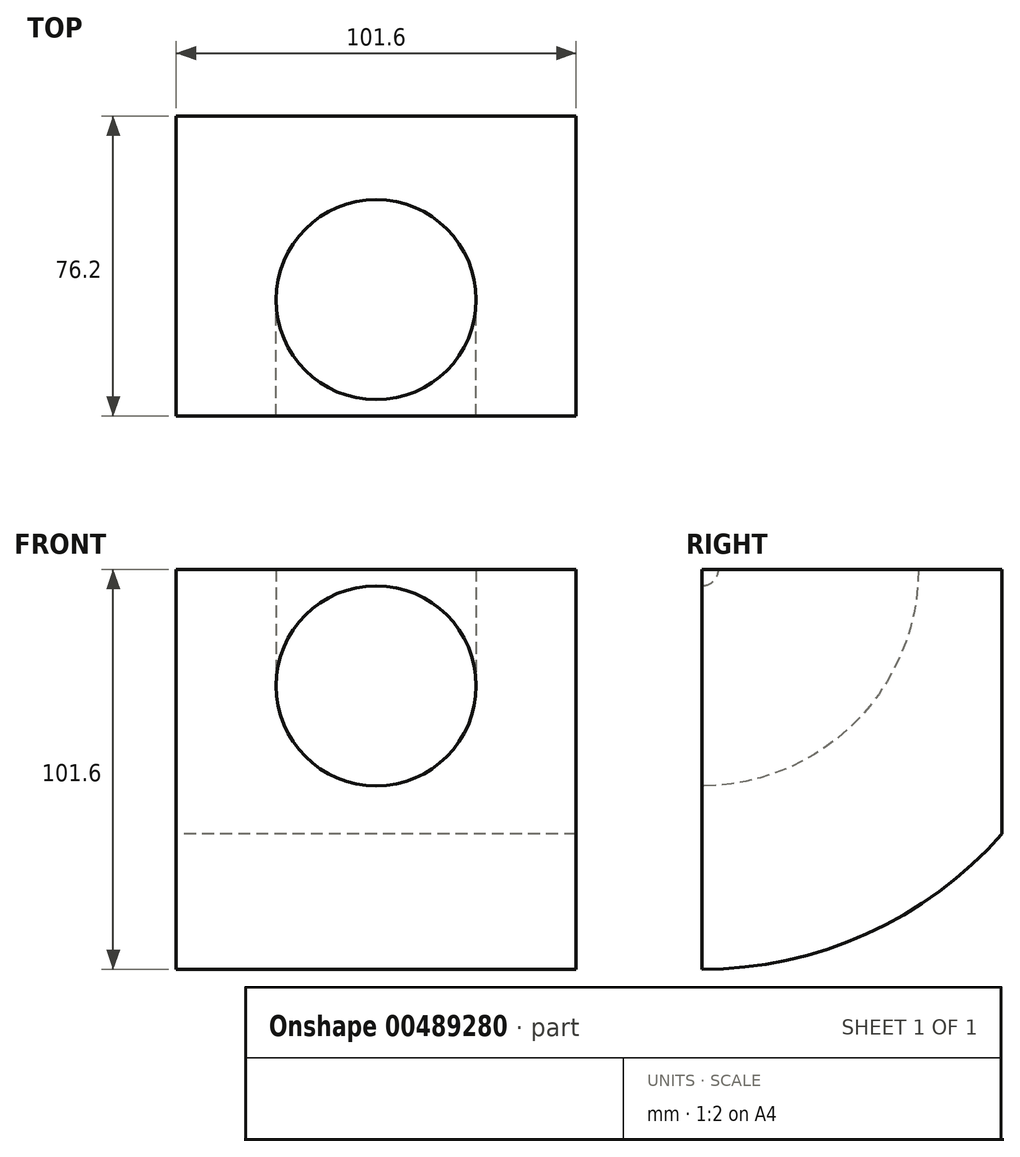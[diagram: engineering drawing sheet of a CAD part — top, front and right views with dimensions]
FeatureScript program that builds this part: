
annotation { "Feature Type Name" : "Feature", "Feature Type Description" : "" }
export const myFeature = defineFeature(function(context is Context, id is Id, definition is map)
    precondition{}
    {
        {
            var Q0;
            Q0=qCreatedBy(makeId("Front.planeOp"),FACE);
            var sketch = newSketch(context, id + "F0", { "sketchPlane" : qUnion([Q0])});
            skLineSegment(sketch, "E0.bottom", {"start": v(50.8, 87.4) * mm, "end": v(-50.8, 87.4) * mm});
            skLineSegment(sketch, "E0.top", {"start": v(50.8, -14.2) * mm, "end": v(-50.8, -14.2) * mm});
            skLineSegment(sketch, "E0.left", {"start": v(50.8, 87.4) * mm, "end": v(50.8, -14.2) * mm});
            skLineSegment(sketch, "E0.right", {"start": v(-50.8, 87.4) * mm, "end": v(-50.8, -14.2) * mm});
            skPoint(sketch, "E0.middle", {"position": v(0, 36.6) * mm});
            skSolve(sketch);
        }
        {
            var Q0;
            Q0=makeQuery(id+"F0.imprint","IMPRINT",FACE,{"disambiguationData":[TD([[makeQuery(id+"F0.imprint","IMPRINT",EDGE,{"derivedFrom":sQuery(id+"F0.wireOp",EDGE,"E0.bottom")}),1.0]])]});
            extrude(context, id + "F1", {"entities" : qUnion([Q0]), "endBound" : BoundingType.SYMMETRIC, "depth" : 76.2 * mm});
        }
        {
            var Q0;
            Q0=makeQuery(id+"F1.opExtrude","CAP_FACE",FACE,{"disambiguationData":[OSD([sQuery(id+"F0.wireOp",EDGE,"E0.bottom"),sQuery(id+"F0.wireOp",EDGE,"E0.top"),sQuery(id+"F0.wireOp",EDGE,"E0.left"),sQuery(id+"F0.wireOp",EDGE,"E0.right")])],"isStart":false});
            var sketch = newSketch(context, id + "F2", { "sketchPlane" : qUnion([Q0])});
            skCircle(sketch, "E1", {"center": v(0, 57.85) * mm, "radius": 25.4 * mm});
            skSolve(sketch);
        }
        {
            var Q0;
            Q0=makeQuery(id+"F2.imprint","IMPRINT",FACE,{"disambiguationData":[TD([[makeQuery(id+"F2.imprint","IMPRINT",EDGE,{"derivedFrom":sQuery(id+"F2.wireOp",EDGE,"E1")}),-1.0]])]});
            var Q1;
            Q1=sQuery(id+"F2.wireOp",EDGE,"E1");
            var Q2;
            Q2=makeQuery(id+"F1.opExtrude","CAP_EDGE",EDGE,{"disambiguationData":[OSD([sQuery(id+"F0.wireOp",EDGE,"E0.bottom")])],"isStart":false});
            revolve(context, id + "F3", {"operationType" : NewBodyOperationType.INTERSECT, "entities" : qUnion([Q0]), "surfaceEntities" : qUnion([Q1]), "axis" : qUnion([Q2]), "revolveType" : RevolveType.FULL, "oppositeDirection" : true});
        }
    });
